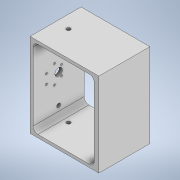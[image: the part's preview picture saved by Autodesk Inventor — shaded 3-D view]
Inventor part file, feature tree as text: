
AUTODESK INVENTOR PART (.ipt)
format: ipt  version: 2020.3 (Build 243373000, 373)  size: 206,848 bytes
history: native  units: mm
features: extrude x9, sketch x9, projected_geometry x3, fillet x2
ambient origin geometry x8: Origin, YZ Plane, XZ Plane, XY Plane, X Axis, Y Axis, Z Axis, Center Point
bodies: Solid1 (feature_tree)
feature tree (23):
  extrude  "Extrusion1"  Depth=130.0mm
  extrude  "Extrusion5"  Depth=5.0mm TaperAngle=0.0deg
  extrude  "Extrusion6"  Depth=140.0mm
  extrude  "Extrusion8"  Depth=70.0mm
  extrude  "Extrusion9"  Depth=2.778mm TaperAngle=0.0deg
  fillet  "Fillet1"  Radius=17.5mm
  fillet  "Fillet2"  Radius=17.5mm
  extrude  "Extrusion10"  Depth=8.0mm
  extrude  "Extrusion12"  Depth=3.3mm
  sketch  "Sketch12"  dims[d33=37.767mm d34=78.237mm]
  sketch  "Sketch13"  dims[d35=3.3mm d36=37.733mm d38=61.753708mm d39=3.3mm d41=85.5mm d42=49.5mm d43=3.3mm d44=54.5mm d45=3.3mm d46=77.75mm d47=62.923mm d48=3.3mm d49=62.25mm d50=62.923mm d51=5.0mm d52=0.0mm d53=6.5mm d54=6.5mm d58=21.5mm d59=21.5mm d60=10.0mm d61=0.0mm d62=6.5mm d63=21.5mm d64=10.0mm d65=0.0mm d66=6.5mm d67=21.5mm d68=10.0mm d69=0.0mm]
  extrude  "Extrusion13"  Depth=78.237mm
  extrude  "Extrusion14"  Depth=10.0mm
  sketch  "Sketch1"  dims[d0=101.968mm d1=130.0mm]
  sketch  "Sketch5"  dims[d2=5.0mm d3=50.0mm d4=0.0mm]
  sketch  "Sketch6"  dims[d14=140.0mm d15=24.0mm]
  projected_geometry  "Projected Loop4"
  sketch  "Sketch8"  dims[d16=25.0mm d17=70.0mm]
  projected_geometry  "Projected Loop5"
  sketch  "Sketch9"  dims[d18=2.778mm d19=0.0mm d20=2.778mm d21=0.0mm d25=17.5mm d26=0.0mm d27=17.5mm d28=0.0mm]
  projected_geometry  "Projected Loop6"
  sketch  "Sketch10"  dims[d29=8.0mm d30=8.0mm]
  sketch  "Sketch11"  dims[d31=12.5mm d32=3.3mm]
